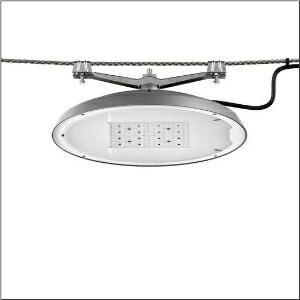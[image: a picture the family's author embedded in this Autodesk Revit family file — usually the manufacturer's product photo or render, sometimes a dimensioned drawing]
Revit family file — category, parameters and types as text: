
# Revit family: dl_r__50_iq_mini___st0_8s_5xa248v41f08me_8e0e
name_source: partatom
category: Lighting Fixtures
units: mm (PartAtom-declared; Revit-internal decimal feet)

## family parameters
Cut with Voids When Loaded = No
Host = Face
Light Source = No
Part Type = Normal
Room Calculation Point = No
Round Connector Dimension = Use Diameter
Shared = No

## types (1)
- --- (1 x LED, 15660 lm, 101.7 W, 4000K)
    Apparent Load = 102 VA
    CIE Flux Codes = 38 75 97 100 100
    Color Rendering = 70
    Color Temperature = 4000K
    Default Elevation = 1800 mm
    Description = DL® 50 iQ mini, catenary luminaire, primary light control with lens, of PMMA, primary optical cover: cover, of toughened safety glass, transparent, light distribution: ST0.8s, light emission: direct distribution, primary light characteristic: symmetric, installation type: suspended mounting, LED, High Power LED, rated luminous flux: 15.660lm, luminous efficacy: 154lm/W, light colour: 740, colour temperature: 4000K, control gear: iQ Street-Remote, control: optimised constant luminous flux control (CLO 2.0), Desk-Remote (wireless, voltage-free reading and setting of iQ features in the workshop via application-optimized NFC function/RFID function), Light-Fading, Smart-Wire, Night-Set, Lumen-Switch, Temp-Guard, Auto-Match, Street-Remote, mains connection: 230..240V, AC, 50/60Hz, start of lifetime: 102W, end of service life: 111W, reduction: 45W, luminaire housing, of diecast aluminium, powder-coated, Siteco® metallic grey (DB 702S), diameter: 500mm, height: 115mm, mounting height: 4..12m, protection rating (complete): IP66, insulation class (complete): insulation class II (safety insulation), certification: CE, ENEC, ENEC+, VDE, impact resistance: IK08, permissible operating ambient temperature for outdoor applications: -25..+40°C, standard-compliant lighting for roads and squares, packaging unit: 1 piece

Light Distribution: ST0.8s
    Height = 124 mm  [stored 0.406824 ft]
    Lamp = 1 x LED
    Lamp Light Flux = 15660 lm
    Lamp Power = 101.7 W
    Lamp count = 1
    Length = 500 mm
    Luminous efficacy = 154 lm/W
    Manufacturer = Siteco
    ModVariant = No
    Model = 5XA248V41F08ME
    Number of Poles = 1
    OnlyDefault = Yes
    Power Factor = 1
    Product Name = DL® 50 iQ mini | ST0.8s
    Product group = catenary luminaire
    ProductGroupID = 6300
    Protection Class = Protection class II
    Protection Degree = IP 66
    RLX_Detail_Level = 1
    RLX_Emergency_Light_Flux = 0 lm
    RLX_Emergency_Type = 0
    RLX_Emergency_Type_DB = No
    RlxData = <blob elided: 127457 chars, md5=c601e175>
    Socket = socket
    Standby Power = 0 W
    System Light Flux = 15660 lm
    System Power = 102 W
    Type Comments = factory setting: luminous flux: 100 % | dim-lin: 254 | 534 mA
    Type Image = l_1251783.jpg
    URL = http://relux.com
    VarID = @adj_162423
    Voltage = 0 V
    Weight = 0.00 kg
    Width = 0 mm  [stored 0 ft]

note: [stored X ft] marks values corroborated as IEEE doubles in the binary element streams (Revit-internal decimal feet)

## geometry (parser evidence)
native form markers: Blend x4, Sweep x15
no freeform markers — native parametric forms only
